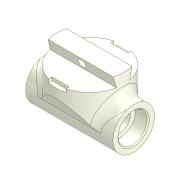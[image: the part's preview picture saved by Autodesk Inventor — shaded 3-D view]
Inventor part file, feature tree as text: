
AUTODESK INVENTOR PART (.ipt)
format: ipt  version: 2022 (Build 260153000, 153)  size: 375,296 bytes
history: native  units: mm
features: sketch x13, extrude x8, hole x5, projected_geometry x5, mirror x3, chamfer x2, plane x2, thicken_offset x1, fillet x1, split x1
ambient origin geometry x8: Origin, YZ Plane, XZ Plane, XY Plane, X Axis, Y Axis, Z Axis, Center Point
bodies: Solid1 (feature_tree), Solid2 (feature_tree), Solid3 (feature_tree)
feature tree (41):
  extrude  "Extrusion1"  Depth=5.0mm TaperAngle=0.0deg
  extrude  "Extrusion2"  Depth=40.0mm TaperAngle=0.0deg
  sketch  "Sketch4"  dims[d9=6.0mm d10=4.0mm d11=2.0mm d12=90.0deg d13=6.0mm d14=0.0mm d15=24.0mm]
  hole  "Hole1"  [1 undecoded]
  mirror  "Mirror1"
  hole  "Hole5"  [1 undecoded]
  thicken_offset  "Thicken1"
  extrude  "Extrusion3"  Depth=5.0mm
  extrude  "Extrusion4"  Depth=4.0mm TaperAngle=45.0deg
  fillet  "Fillet1"  Radius=0.2mm
  hole  "Hole2"  [1 undecoded]
  hole  "Hole3"  [1 undecoded]
  chamfer  "Chamfer1"  [1 undecoded]
  chamfer  "Chamfer2"  Distance=15.5mm
  plane  "Work Plane1"
  split  "Split1"
  extrude  "Extrusion8"  Depth=8.0mm
  extrude  "Extrusion10"  Depth=8.0mm
  plane  "Work Plane5"
  hole  "Hole9"  [1 undecoded]
  extrude  "Extrusion11"  Depth=8.0mm
  mirror  "Mirror2"
  extrude  "Extrusion12"  TaperAngle=0.0deg  [1 undecoded]
  mirror  "Mirror3"
  sketch  "Sketch1"  dims[d1=5.0mm d2=24.25mm d3=0.0mm]
  sketch  "Sketch2"  dims[d5=3.0mm d6=40.0mm d7=0.0mm]
  sketch  "Sketch3"  dims[d8=13.0mm]
  sketch  "Sketch5"  dims[d16=5.0mm d17=0.0mm d18=0.0mm d19=0.0mm]
  sketch  "Sketch6"  dims[d20=5.0mm d21=15.0mm]
  sketch  "Sketch7"  dims[d22=40.0mm d24=360.0deg]
  sketch  "Sketch9"  dims[d26=2.0mm d27=6.0mm d28=4.0mm d29=2.0mm d30=90.0deg d31=5.0mm d32=20.594885mm]
  sketch  "Sketch21"  dims[d33=10.0mm d34=6.0mm d35=4.0mm d36=2.0mm d37=90.0deg d38=2.0mm d39=0.0mm d40=2.0mm d41=2.0mm d42=45.0deg d50=0.2mm d51=0.15mm]
  sketch  "Sketch23"  dims[d52=9.0mm d53=6.0mm d54=4.0mm d55=2.0mm d56=90.0deg d57=6.0mm d58=0.0mm d59=0.5mm d60=2.0mm d61=45.0deg]
  sketch  "Sketch24"  dims[d62=-7.0mm d105=5.0mm d106=0.0mm]
  projected_geometry  "Projected Loop2"
  sketch  "Sketch25"  dims[d110=9.0mm]
  sketch  "Sketch26"  dims[d112=6.5mm d113=0.0mm d114=0.0mm d115=15.5mm d116=3.4mm d117=6.0mm d118=4.0mm d119=2.0mm d120=90.0deg d121=8.0mm d122=20.594885mm d123=8.0mm d124=8.0mm d125=2.0mm d126=0.0mm d127=0.2mm d128=0.0mm d129=0.0mm d43=0.15mm d44=0.25mm d45=0.375mm d46=14.3117mm d47=0.75mm d48=20.594885mm d49=0.0625mm]
  projected_geometry  "Project Cut Edges1"
  projected_geometry  "Project Cut Edges2"
  projected_geometry  "Project Cut Edges3"
  projected_geometry  "Project Cut Edges4"
note: 7 required parameter values undecoded (feature->parameter linkage not recoverable at this tier; creation-order binding heuristic only, values carry confidence <= 0.55)
